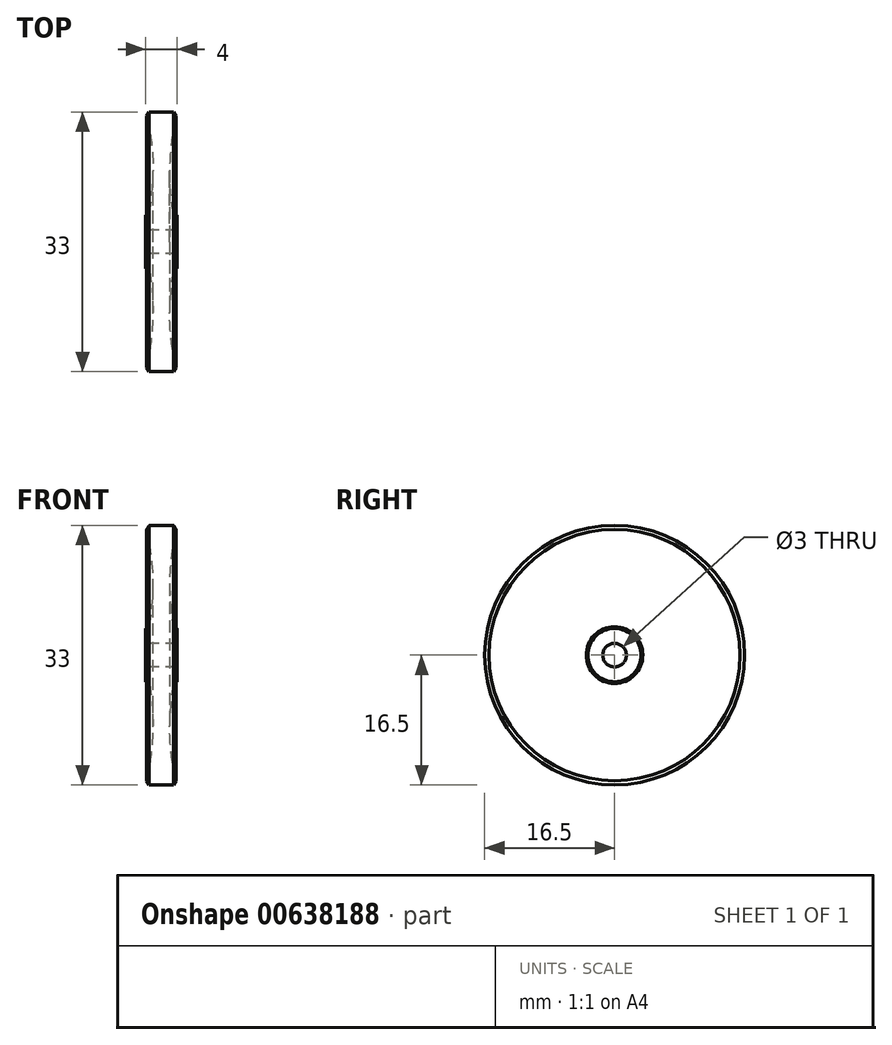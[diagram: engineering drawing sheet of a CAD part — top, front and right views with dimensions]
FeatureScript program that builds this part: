
annotation { "Feature Type Name" : "Feature", "Feature Type Description" : "" }
export const myFeature = defineFeature(function(context is Context, id is Id, definition is map)
    precondition{}
    {
        {
            var Q0;
            Q0=qCreatedBy(makeId("Top.planeOp"),FACE);
            var sketch = newSketch(context, id + "F0", { "sketchPlane" : qUnion([Q0])});
            skLineSegment(sketch, "E0.bottom", {"start": v(0, 1.5) * mm, "end": v(2, 1.5) * mm});
            skLineSegment(sketch, "E0.top", {"start": v(0, 16.5) * mm, "end": v(1.55, 16.5) * mm});
            skLineSegment(sketch, "E0.left", {"start": v(0, 1.5) * mm, "end": v(0, 16.5) * mm});
            skLineSegment(sketch, "E0.right", {"start": v(2, 1.5) * mm, "end": v(2, 3.38) * mm});
            skArc(sketch, "E1", {"start": v(1.86, 15.95) * mm, "mid": v(1.06, 9.8) * mm, "end": v(1.54, 3.6) * mm});
            skLineSegment(sketch, "E2", {"start": v(1.55, 16.5) * mm, "end": v(1.86, 15.95) * mm});
            skLineSegment(sketch, "E3", {"start": v(1.54, 3.6) * mm, "end": v(2, 3.38) * mm});
            skPoint(sketch, "E4.orphan", {"position": v(2, 16.5) * mm});
            skArc(sketch, "E5.MirrorCS", {"start": v(-1.86, 15.95) * mm, "mid": v(-1.06, 9.8) * mm, "end": v(-1.54, 3.6) * mm});
            skLineSegment(sketch, "E6.MirrorCS", {"start": v(0, 1.5) * mm, "end": v(-2, 1.5) * mm});
            skLineSegment(sketch, "E7.MirrorCS", {"start": v(-2, 1.5) * mm, "end": v(-2, 3.38) * mm});
            skLineSegment(sketch, "E8.MirrorCS", {"start": v(-1.54, 3.6) * mm, "end": v(-2, 3.38) * mm});
            skLineSegment(sketch, "E9.MirrorCS", {"start": v(0, 16.5) * mm, "end": v(-1.55, 16.5) * mm});
            skLineSegment(sketch, "E10.MirrorCS", {"start": v(-1.55, 16.5) * mm, "end": v(-1.86, 15.95) * mm});
            skLineSegment(sketch, "E11", {"start": v(-6.78, 0) * mm, "end": v(8.09, 0) * mm, "construction": true});
            skSolve(sketch);
        }
        {
            var Q0;
            Q0=makeQuery(id+"F0.imprint","IMPRINT",FACE,{"disambiguationData":[TD([[makeQuery(id+"F0.imprint","IMPRINT",EDGE,{"derivedFrom":sQuery(id+"F0.wireOp",EDGE,"E0.bottom")}),1.0]])]});
            var Q1;
            Q1=makeQuery(id+"F0.imprint","IMPRINT",FACE,{"disambiguationData":[TD([[makeQuery(id+"F0.imprint","IMPRINT",EDGE,{"derivedFrom":sQuery(id+"F0.wireOp",EDGE,"E0.left")}),1.0]])]});
            var Q2;
            Q2=sQuery(id+"F0.wireOp",EDGE,"E11");
            revolve(context, id + "F1", {"entities" : qUnion([Q0, Q1]), "axis" : qUnion([Q2]), "revolveType" : RevolveType.FULL});
        }
    });
